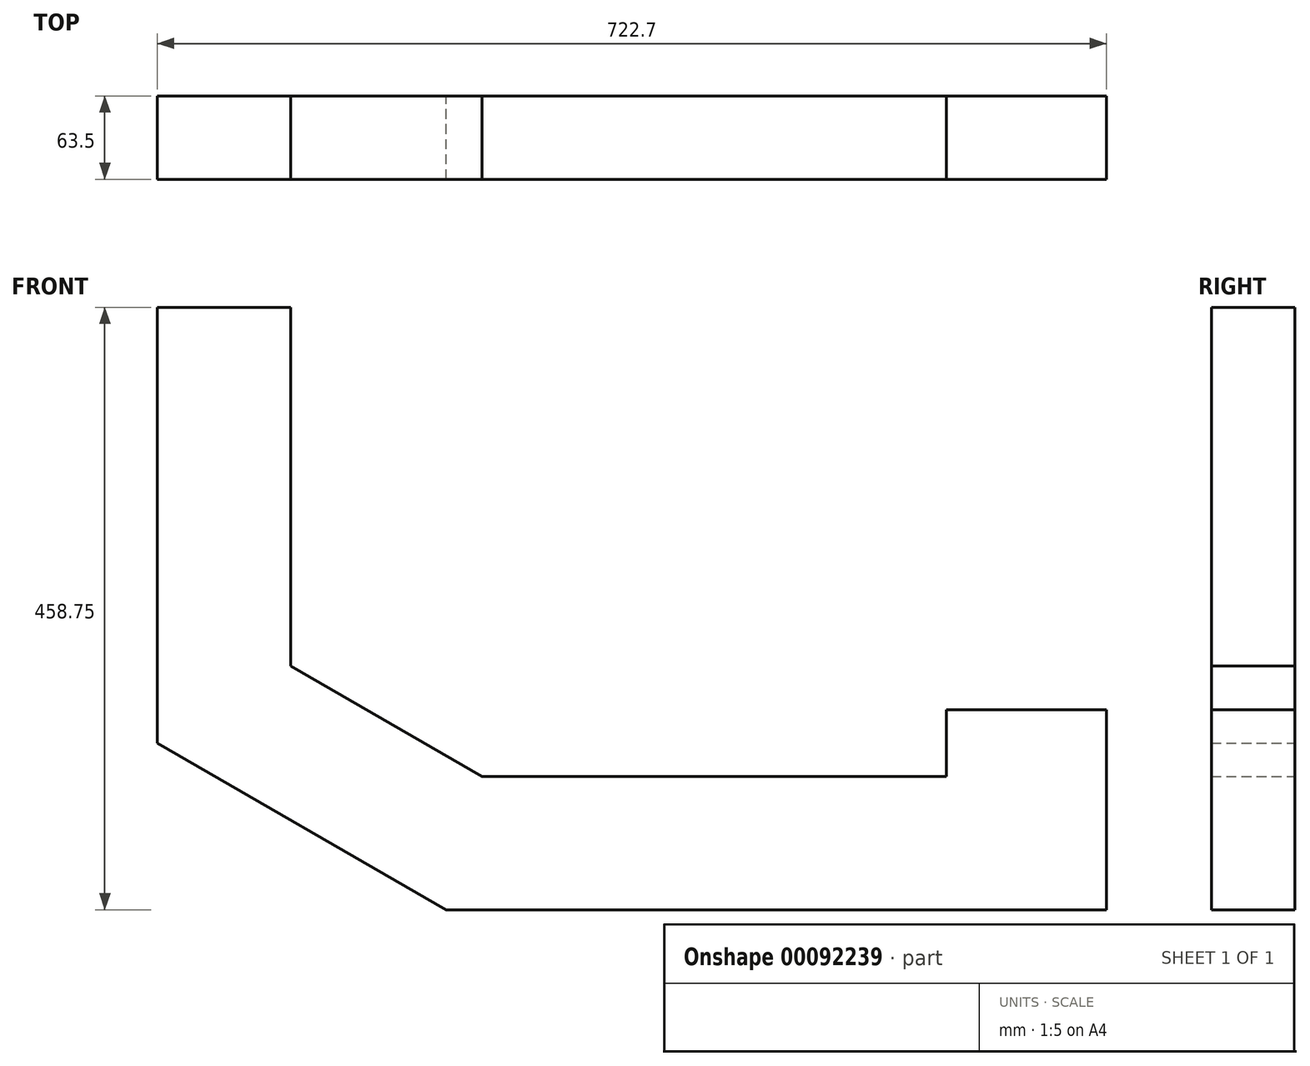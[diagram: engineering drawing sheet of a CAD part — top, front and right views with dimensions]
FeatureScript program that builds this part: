
annotation { "Feature Type Name" : "Feature", "Feature Type Description" : "" }
export const myFeature = defineFeature(function(context is Context, id is Id, definition is map)
    precondition{}
    {
        {
            var Q0;
            Q0=qCreatedBy(makeId("Front.planeOp"),FACE);
            var sketch = newSketch(context, id + "F0", { "sketchPlane" : qUnion([Q0])});
            skLineSegment(sketch, "E0.bottom", {"start": v(-914.4, 0) * mm, "end": v(0, 0) * mm});
            skLineSegment(sketch, "E0.top", {"start": v(-914.4, 914.4) * mm, "end": v(0, 914.4) * mm});
            skLineSegment(sketch, "E0.left", {"start": v(-914.4, 0) * mm, "end": v(-914.4, 914.4) * mm});
            skLineSegment(sketch, "E0.right", {"start": v(0, 0) * mm, "end": v(0, 914.4) * mm});
            skLineSegment(sketch, "E1.bottom", {"start": v(0, 914.4) * mm, "end": v(609.6, 914.4) * mm});
            skLineSegment(sketch, "E1.top", {"start": v(0, 863.6) * mm, "end": v(609.6, 863.6) * mm});
            skLineSegment(sketch, "E1.left", {"start": v(0, 914.4) * mm, "end": v(0, 863.6) * mm});
            skLineSegment(sketch, "E1.right", {"start": v(609.6, 914.4) * mm, "end": v(609.6, 863.6) * mm});
            skSolve(sketch);
        }
        {
            var Q0;
            Q0=qCreatedBy(makeId("Front.planeOp"),FACE);
            var sketch = newSketch(context, id + "F1", { "sketchPlane" : qUnion([Q0])});
            skLineSegment(sketch, "E2.bottom", {"start": v(297.58, 806.8) * mm, "end": v(399.18, 806.8) * mm});
            skLineSegment(sketch, "E3", {"start": v(297.58, 806.8) * mm, "end": v(297.58, 475.05) * mm});
            skLineSegment(sketch, "E4", {"start": v(297.58, 475.05) * mm, "end": v(517.55, 348.05) * mm});
            skLineSegment(sketch, "E5", {"start": v(399.18, 806.8) * mm, "end": v(399.18, 533.71) * mm});
            skLineSegment(sketch, "E6", {"start": v(399.18, 533.71) * mm, "end": v(544.77, 449.65) * mm});
            skLineSegment(sketch, "E7", {"start": v(517.55, 348.05) * mm, "end": v(898.55, 348.05) * mm});
            skLineSegment(sketch, "E8", {"start": v(544.77, 449.65) * mm, "end": v(898.55, 449.65) * mm});
            skLineSegment(sketch, "E9", {"start": v(898.55, 449.65) * mm, "end": v(898.55, 500.45) * mm});
            skLineSegment(sketch, "E10", {"start": v(898.55, 348.05) * mm, "end": v(1020.28, 348.05) * mm});
            skLineSegment(sketch, "E11", {"start": v(1020.28, 348.05) * mm, "end": v(1020.28, 500.45) * mm});
            skLineSegment(sketch, "E12", {"start": v(1020.28, 500.45) * mm, "end": v(898.55, 500.45) * mm});
            skSolve(sketch);
        }
        {
            var Q0;
            Q0 = qSketchRegion(id + "F1", true);
            extrude(context, id + "F2", {"entities" : qUnion([Q0]), "depth" : 63.5 * mm});
        }
    });
